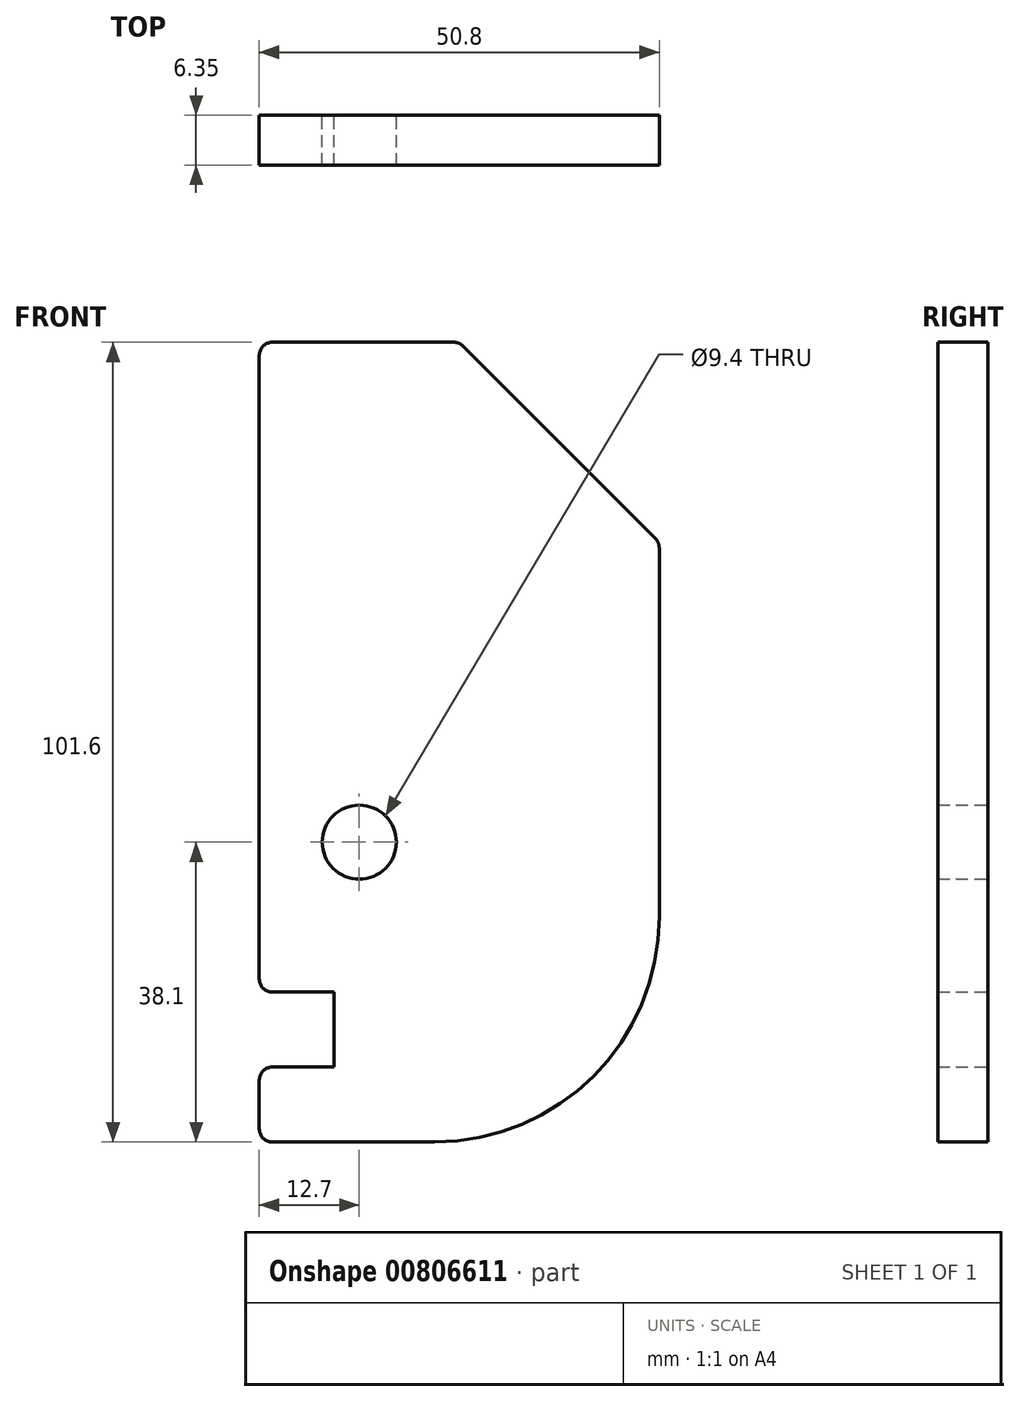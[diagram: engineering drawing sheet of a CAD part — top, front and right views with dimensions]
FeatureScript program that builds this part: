
annotation { "Feature Type Name" : "Feature", "Feature Type Description" : "" }
export const myFeature = defineFeature(function(context is Context, id is Id, definition is map)
    precondition{}
    {
        {
            var Q0;
            Q0=qCreatedBy(makeId("Front.planeOp"),FACE);
            var sketch = newSketch(context, id + "F0", { "sketchPlane" : qUnion([Q0])});
            skLineSegment(sketch, "E0.bottom", {"start": v(0, 28.58) * mm, "end": v(0, 75.52) * mm});
            skLineSegment(sketch, "E0.top", {"start": v(-50.8, 1.65) * mm, "end": v(-50.8, 7.87) * mm});
            skLineSegment(sketch, "E0.left", {"start": v(-28.57, 0) * mm, "end": v(-49.15, 0) * mm});
            skLineSegment(sketch, "E0.right", {"start": v(-26.08, 101.6) * mm, "end": v(-49.15, 101.6) * mm});
            skPoint(sketch, "E1.visualSharp", {"position": v(0, 0) * mm});
            skArc(sketch, "E1.filletArc", {"start": v(-28.57, 0) * mm, "mid": v(-8.37, 8.37) * mm, "end": v(0, 28.57) * mm});
            skCircle(sketch, "E2", {"center": v(-38.1, 38.1) * mm, "radius": 4.7 * mm});
            skLineSegment(sketch, "E3", {"start": v(-49.15, 9.52) * mm, "end": v(-41.27, 9.52) * mm});
            skLineSegment(sketch, "E4", {"start": v(-41.27, 9.52) * mm, "end": v(-41.27, 19.05) * mm});
            skLineSegment(sketch, "E5", {"start": v(-41.27, 19.05) * mm, "end": v(-49.15, 19.05) * mm});
            skLineSegment(sketch, "E6.trimOffspring", {"start": v(-50.8, 20.7) * mm, "end": v(-50.8, 99.95) * mm});
            skLineSegment(sketch, "E7", {"start": v(-0.48, 76.68) * mm, "end": v(-24.92, 101.12) * mm});
            skPoint(sketch, "E8.orphan", {"position": v(0, 101.6) * mm});
            skPoint(sketch, "E9.visualSharp", {"position": v(0, 76.2) * mm});
            skArc(sketch, "E9.filletArc", {"start": v(0, 75.52) * mm, "mid": v(-0.13, 76.15) * mm, "end": v(-0.48, 76.68) * mm});
            skPoint(sketch, "E10.visualSharp", {"position": v(-25.4, 101.6) * mm});
            skArc(sketch, "E10.filletArc", {"start": v(-24.92, 101.12) * mm, "mid": v(-25.45, 101.47) * mm, "end": v(-26.08, 101.6) * mm});
            skPoint(sketch, "E11.visualSharp", {"position": v(-50.8, 101.6) * mm});
            skArc(sketch, "E11.filletArc", {"start": v(-49.15, 101.6) * mm, "mid": v(-50.32, 101.12) * mm, "end": v(-50.8, 99.95) * mm});
            skPoint(sketch, "E12.visualSharp", {"position": v(-50.8, 19.05) * mm});
            skArc(sketch, "E12.filletArc", {"start": v(-50.8, 20.7) * mm, "mid": v(-50.32, 19.53) * mm, "end": v(-49.15, 19.05) * mm});
            skPoint(sketch, "E13.visualSharp", {"position": v(-50.8, 9.52) * mm});
            skArc(sketch, "E13.filletArc", {"start": v(-49.15, 9.52) * mm, "mid": v(-50.32, 9.04) * mm, "end": v(-50.8, 7.87) * mm});
            skPoint(sketch, "E14.visualSharp", {"position": v(-50.8, 0) * mm});
            skArc(sketch, "E14.filletArc", {"start": v(-50.8, 1.65) * mm, "mid": v(-50.32, 0.48) * mm, "end": v(-49.15, 0) * mm});
            skSolve(sketch);
        }
        {
            var Q0;
            Q0 = qSketchRegion(id + "F0", true);
            extrude(context, id + "F1", {"entities" : qUnion([Q0]), "depth" : 6.35 * mm, "offsetDistance" : 25.4 * mm});
        }
    });
